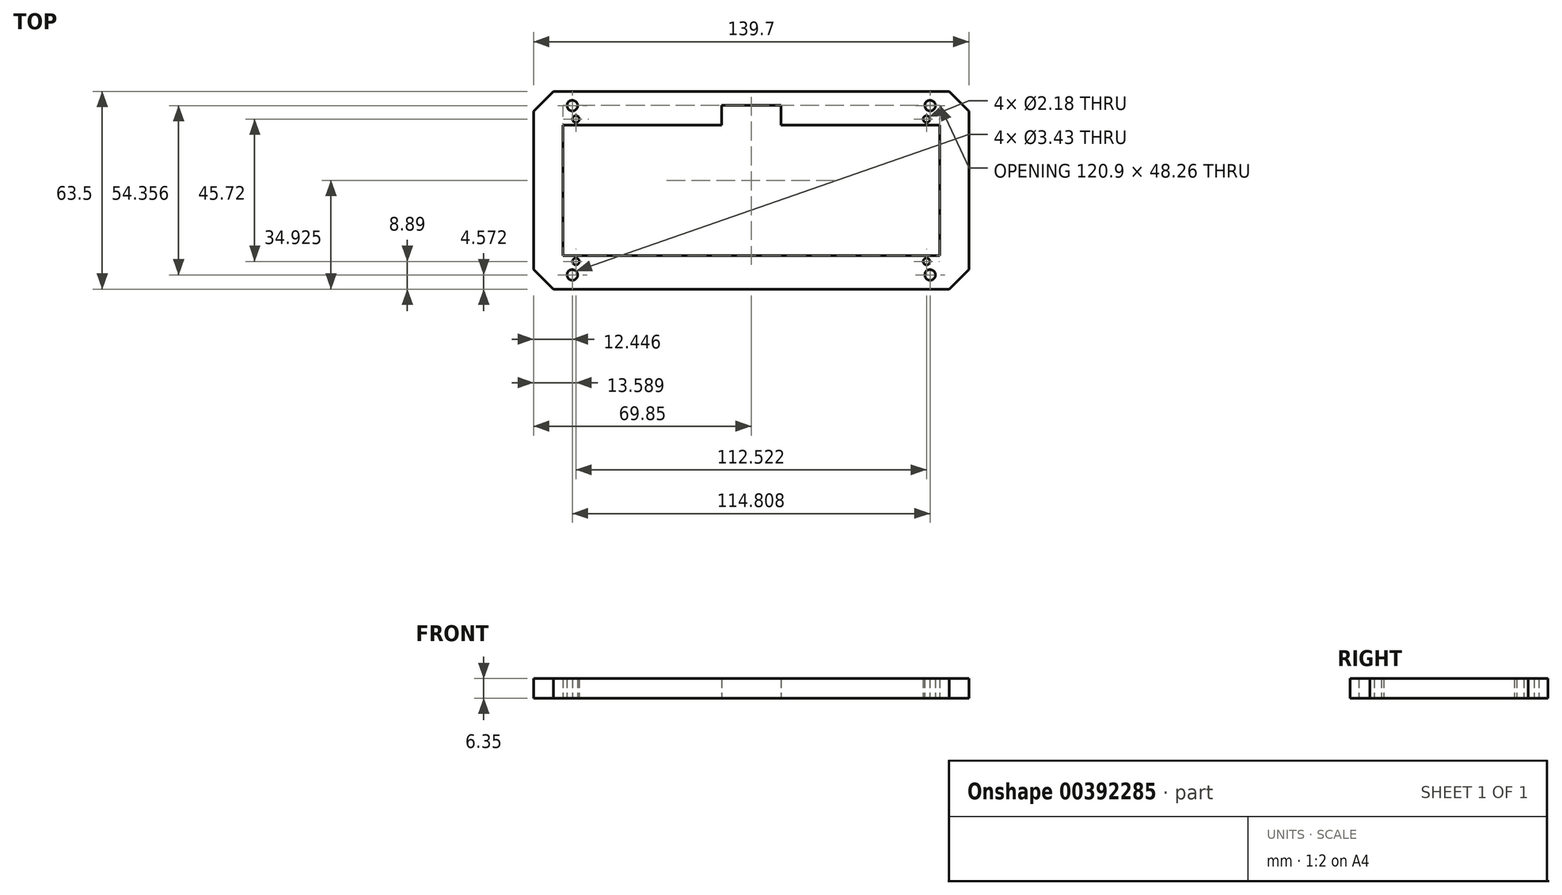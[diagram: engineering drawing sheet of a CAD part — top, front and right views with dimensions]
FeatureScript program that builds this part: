
annotation { "Feature Type Name" : "Feature", "Feature Type Description" : "" }
export const myFeature = defineFeature(function(context is Context, id is Id, definition is map)
    precondition{}
    {
        {
            var Q0;
            Q0=qCreatedBy(makeId("Top.planeOp"),FACE);
            var sketch = newSketch(context, id + "F0", { "sketchPlane" : qUnion([Q0])});
            skLineSegment(sketch, "E0.bottom", {"start": v(57.4, 27.18) * mm, "end": v(-57.4, 27.18) * mm, "construction": true});
            skLineSegment(sketch, "E0.top", {"start": v(57.4, -27.18) * mm, "end": v(-57.4, -27.18) * mm, "construction": true});
            skLineSegment(sketch, "E0.left", {"start": v(57.4, 27.18) * mm, "end": v(57.4, -27.18) * mm, "construction": true});
            skLineSegment(sketch, "E0.right", {"start": v(-57.4, 27.18) * mm, "end": v(-57.4, -27.18) * mm, "construction": true});
            skPoint(sketch, "E0.middle", {"position": v(0, 0) * mm});
            skLineSegment(sketch, "E1.bottom", {"start": v(60.45, 20.96) * mm, "end": v(-60.45, 20.96) * mm});
            skLineSegment(sketch, "E1.top", {"start": v(60.45, -20.96) * mm, "end": v(-60.45, -20.96) * mm});
            skLineSegment(sketch, "E1.left", {"start": v(60.45, 20.96) * mm, "end": v(60.45, -20.96) * mm});
            skLineSegment(sketch, "E1.right", {"start": v(-60.45, 20.96) * mm, "end": v(-60.45, -20.96) * mm});
            skLineSegment(sketch, "E2.bottom", {"start": v(56.26, 22.86) * mm, "end": v(-56.26, 22.86) * mm, "construction": true});
            skLineSegment(sketch, "E2.top", {"start": v(56.26, -22.86) * mm, "end": v(-56.26, -22.86) * mm, "construction": true});
            skLineSegment(sketch, "E2.left", {"start": v(56.26, 22.86) * mm, "end": v(56.26, -22.86) * mm, "construction": true});
            skLineSegment(sketch, "E2.right", {"start": v(-56.26, 22.86) * mm, "end": v(-56.26, -22.86) * mm, "construction": true});
            skLineSegment(sketch, "E3.bottom", {"start": v(69.85, 31.75) * mm, "end": v(-69.85, 31.75) * mm});
            skLineSegment(sketch, "E3.top", {"start": v(69.85, -31.75) * mm, "end": v(-69.85, -31.75) * mm});
            skLineSegment(sketch, "E3.left", {"start": v(69.85, 31.75) * mm, "end": v(69.85, -31.75) * mm});
            skLineSegment(sketch, "E3.right", {"start": v(-69.85, 31.75) * mm, "end": v(-69.85, -31.75) * mm});
            skCircle(sketch, "E4", {"center": v(-57.4, 27.18) * mm, "radius": 1.71 * mm});
            skCircle(sketch, "E5", {"center": v(-56.26, 22.86) * mm, "radius": 1.1 * mm});
            skCircle(sketch, "E6", {"center": v(-57.4, -27.18) * mm, "radius": 1.71 * mm});
            skCircle(sketch, "E7", {"center": v(57.4, -27.18) * mm, "radius": 1.71 * mm});
            skCircle(sketch, "E8", {"center": v(56.26, -22.86) * mm, "radius": 1.1 * mm});
            skCircle(sketch, "E9", {"center": v(57.4, 27.18) * mm, "radius": 1.71 * mm});
            skCircle(sketch, "E10", {"center": v(56.26, 22.86) * mm, "radius": 1.1 * mm});
            skCircle(sketch, "E11", {"center": v(-56.26, -22.86) * mm, "radius": 1.1 * mm});
            skLineSegment(sketch, "E12.top", {"start": v(-9.52, 27.3) * mm, "end": v(9.53, 27.3) * mm});
            skLineSegment(sketch, "E12.left", {"start": v(-9.53, 20.96) * mm, "end": v(-9.53, 27.3) * mm});
            skLineSegment(sketch, "E12.right", {"start": v(9.52, 20.96) * mm, "end": v(9.52, 27.3) * mm});
            skPoint(sketch, "E12.middle", {"position": v(0, 20.96) * mm});
            skSolve(sketch);
        }
        {
            var Q0;
            Q0=makeQuery(id+"F0.imprint","IMPRINT",FACE,{"disambiguationData":[TD([[makeQuery(id+"F0.imprint","IMPRINT",EDGE,{"derivedFrom":sQuery(id+"F0.wireOp",EDGE,"E1.top")}),1.0]])]});
            extrude(context, id + "F1", {"entities" : qUnion([Q0]), "depth" : 6.35 * mm});
        }
        {
            var Q0;
            Q0=makeQuery(id+"F1.opExtrude","SWEPT_EDGE",EDGE,{"disambiguationData":[OSD([sQuery(id+"F0.wireOp",EDGE,"E3.top"),sQuery(id+"F0.wireOp",EDGE,"E3.right")])]});
            var Q1;
            Q1=makeQuery(id+"F1.opExtrude","SWEPT_EDGE",EDGE,{"disambiguationData":[OSD([sQuery(id+"F0.wireOp",EDGE,"E3.bottom"),sQuery(id+"F0.wireOp",EDGE,"E3.left")])]});
            var Q2;
            Q2=makeQuery(id+"F1.opExtrude","SWEPT_EDGE",EDGE,{"disambiguationData":[OSD([sQuery(id+"F0.wireOp",EDGE,"E3.bottom"),sQuery(id+"F0.wireOp",EDGE,"E3.right")])]});
            var Q3;
            Q3=makeQuery(id+"F1.opExtrude","SWEPT_EDGE",EDGE,{"disambiguationData":[OSD([sQuery(id+"F0.wireOp",EDGE,"E3.top"),sQuery(id+"F0.wireOp",EDGE,"E3.left")])]});
            chamfer(context, id + "F2", {"entities" : qUnion([Q0, Q1, Q2, Q3]), "width" : 6.35 * mm, "tangentPropagation" : true});
        }
    });
